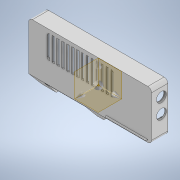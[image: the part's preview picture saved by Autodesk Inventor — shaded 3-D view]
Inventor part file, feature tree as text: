
AUTODESK INVENTOR PART (.ipt)
format: ipt  version: 2021 (Build 250183000, 183)  size: 615,424 bytes
history: native  units: mm
features: sketch x26, extrude x25, chamfer x6, fillet x5, hole x1
ambient origin geometry x8: Origin, YZ Plane, XZ Plane, XY Plane, X Axis, Y Axis, Z Axis, Center Point
bodies: Solid1 (feature_tree)
feature tree (63):
  extrude  "Extrusion1"  Depth=100.0mm
  extrude  "Extrusion3"  Depth=50.0mm
  extrude  "Extrusion4"  Depth=12.5mm
  extrude  "Extrusion12"  Depth=3.0mm TaperAngle=0.0deg
  extrude  "Extrusion13"  Depth=3.0mm TaperAngle=0.0deg
  fillet  "Fillet3"  Radius=2.0mm
  extrude  "Extrusion15"  Depth=2.0mm
  extrude  "Extrusion20"  Depth=44.0mm
  extrude  "Extrusion21"  Depth=12.0mm TaperAngle=0.0deg
  extrude  "Extrusion22"  Depth=12.6mm
  extrude  "Extrusion23"  Depth=3.0mm
  extrude  "Extrusion26"  Depth=4.4mm TaperAngle=0.0deg
  hole  "Hole2"  [1 undecoded]
  chamfer  "Chamfer5"  Distance=12.0mm
  chamfer  "Chamfer7"  Distance=12.0mm
  extrude  "Extrusion27"  Depth=8.0mm
  fillet  "Fillet4"  Radius=8.0mm
  extrude  "Extrusion28"  Depth=2.0mm TaperAngle=0.0deg
  extrude  "Extrusion29"  Depth=10.0mm
  extrude  "Extrusion30"  Depth=8.0mm
  fillet  "Fillet5"  Radius=8.0mm
  extrude  "Extrusion34"  Depth=2.0mm TaperAngle=0.0deg
  extrude  "Extrusion35"  Depth=3.0mm
  extrude  "Extrusion36"  Depth=50.0mm
  extrude  "Extrusion37"  Depth=15.0mm
  fillet  "Fillet6"  Radius=3.0mm
  extrude  "Extrusion38"  Depth=97.0mm
  extrude  "Extrusion39"  Depth=49.0mm
  chamfer  "Chamfer8"  Distance=5.0mm
  extrude  "Extrusion40"  Depth=2.0mm TaperAngle=45.0deg
  fillet  "Fillet7"  Radius=0.8mm
  extrude  "Extrusion41"  Depth=0.5mm
  chamfer  "Chamfer9"  Distance=2.0mm
  chamfer  "Chamfer10"  Distance=2.0mm
  extrude  "Extrusion42"  Depth=2.0mm
  extrude  "Extrusion43"  Depth=24.0mm
  chamfer  "Chamfer11"  Distance=2.0mm
  sketch  "Sketch1"  dims[d0=52.0mm d1=100.0mm]
  sketch  "Sketch4"  dims[d2=26.0mm d3=50.0mm]
  sketch  "Sketch5"  dims[d4=1.2mm d5=0.0mm d35=12.5mm]
  sketch  "Sketch13"  dims[d36=63.1mm d37=3.0mm d38=0.0mm]
  sketch  "Sketch14"  dims[d39=50.673mm d40=3.0mm d41=0.0mm d79=2.0mm]
  sketch  "Sketch16"  dims[d80=2.0mm d81=2.0mm]
  sketch  "Sketch21"  dims[d82=1.2mm d83=44.0mm]
  sketch  "Sketch22"  dims[d84=59.0mm d85=12.0mm d86=0.0mm]
  sketch  "Sketch23"  dims[d87=2.0mm d88=12.6mm]
  sketch  "Sketch24"  dims[d89=12.0mm d90=0.0mm d91=3.0mm]
  sketch  "Sketch27"  dims[d95=33.8mm d96=4.4mm d97=0.0mm]
  sketch  "Sketch28"  dims[d117=2.0mm d118=2.0mm d119=12.0mm d120=0.0mm d121=12.0mm d122=0.0mm]
  sketch  "Sketch29"  dims[d123=70.0mm d124=89.0mm d125=8.0mm]
  sketch  "Sketch30"  dims[d126=8.0mm d127=2.0mm d128=0.0mm]
  sketch  "Sketch31"  dims[d129=8.0mm d130=10.0mm]
  sketch  "Sketch32"  dims[d131=12.0mm d132=8.0mm d133=8.0mm]
  sketch  "Sketch36"  dims[d134=8.0mm d135=2.0mm d136=0.0mm]
  sketch  "Sketch37"  dims[d144=3.0mm d145=3.0mm]
  sketch  "Sketch38"  dims[d146=3.0mm d147=50.0mm]
  sketch  "Sketch39"  dims[d148=97.0mm d149=15.0mm d150=3.0mm]
  sketch  "Sketch40"  dims[d151=3.0mm d152=97.0mm]
  sketch  "Sketch41"  dims[d153=49.0mm d154=4.8mm]
  sketch  "Sketch43"  dims[d155=4.8mm]
  sketch  "Sketch45"  dims[d156=4.8mm]
  sketch  "Sketch46"  dims[d157=4.8mm]
  sketch  "Sketch47"  dims[d158=4.8mm d159=5.0mm d160=0.0mm d161=2.0mm d162=6.0mm d163=4.0mm d164=2.0mm d165=90.0deg d166=4.0mm d167=20.594885mm d174=2.0mm d175=2.0mm d176=45.0deg d180=0.8mm d181=2.0mm d182=45.0deg d184=68.0mm d189=2.0mm d190=0.0mm d191=2.0mm d192=2.0mm d193=24.0mm d194=2.0mm d195=0.0mm d196=36.5mm d197=46.5mm d198=3.5mm d199=2.0mm d200=0.0mm d201=12.5mm d202=23.0mm d203=3.5mm d204=2.0mm d205=0.0mm d206=1.0mm d217=7.6mm d218=10.0mm d219=46.4mm d220=20.0mm d221=0.0mm d222=22.68928mm d223=67.0mm d224=0.0mm d225=1.2mm d226=0.0mm d227=1.2mm d228=0.0mm d229=3.0mm d230=12.3mm d231=33.2mm d232=1.0mm d233=10.0mm d234=1.2mm d235=0.0mm d236=1.2mm d237=5.0mm d238=20.0mm d239=1.5mm d240=0.0mm d241=1.5mm d242=2.0mm d243=45.0deg d245=2.711255mm d246=12.0mm d247=33.2mm d248=3.0mm d249=0.0mm d251=2.0mm d252=1.2mm d253=10.0mm d254=1.5mm d255=0.0mm d256=1.5mm d257=2.0mm d258=45.0deg d259=3.35mm d260=2.0mm d261=45.0deg d262=1.6mm d263=2.0mm d264=0.0mm d265=2.0mm d266=0.0mm d267=1.3mm d268=2.0mm d269=45.0deg d67=0.5mm d68=0.872665mm d69=0.5mm d70=0.872665mm d71=0.5mm d72=0.872665mm d73=0.5mm d74=0.872665mm d75=0.872665mm d76=0.5mm d77=0.872665mm d208=0.5mm d209=0.872665mm d210=0.5mm d211=0.872665mm]
note: 1 required parameter value undecoded (feature->parameter linkage not recoverable at this tier; creation-order binding heuristic only, values carry confidence <= 0.55)
